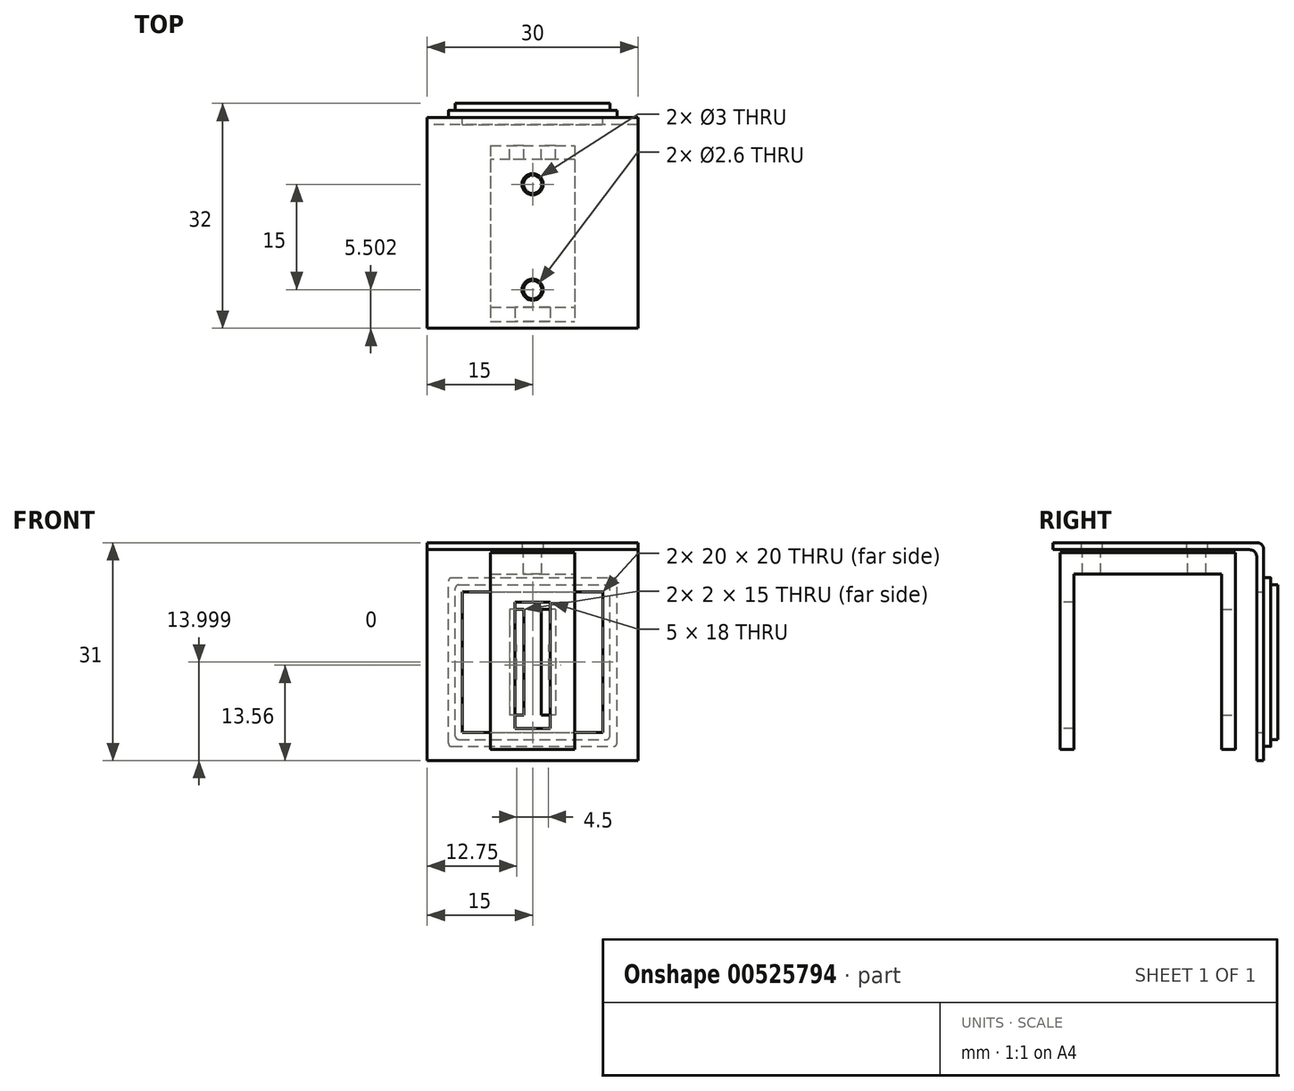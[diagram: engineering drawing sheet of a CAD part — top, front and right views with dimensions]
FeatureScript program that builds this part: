
annotation { "Feature Type Name" : "Feature", "Feature Type Description" : "" }
export const myFeature = defineFeature(function(context is Context, id is Id, definition is map)
    precondition{}
    {
        {
            var Q0;
            Q0=qCreatedBy(makeId("Right.planeOp"),FACE);
            var sketch = newSketch(context, id + "F0", { "sketchPlane" : qUnion([Q0])});
            skLineSegment(sketch, "E0.bottom", {"start": v(-2.16, 1.44) * mm, "end": v(27.84, 1.44) * mm});
            skLineSegment(sketch, "E0.top", {"start": v(-2.16, 0.44) * mm, "end": v(27.84, 0.44) * mm});
            skLineSegment(sketch, "E0.left", {"start": v(-2.16, 1.44) * mm, "end": v(-2.16, 0.44) * mm});
            skLineSegment(sketch, "E0.right", {"start": v(27.84, 1.44) * mm, "end": v(27.84, 0.44) * mm});
            skLineSegment(sketch, "E1.bottom", {"start": v(27.84, 0.44) * mm, "end": v(26.84, 0.44) * mm});
            skLineSegment(sketch, "E1.top", {"start": v(27.84, -29.56) * mm, "end": v(26.84, -29.56) * mm});
            skLineSegment(sketch, "E1.left", {"start": v(27.84, 0.44) * mm, "end": v(27.84, -29.56) * mm});
            skLineSegment(sketch, "E1.right", {"start": v(26.84, 0.44) * mm, "end": v(26.84, -29.56) * mm});
            skSolve(sketch);
        }
        {
            var Q0;
            Q0=qSketchRegion(id+"F0",true);
            extrude(context, id + "F1", {"entities" : qUnion([Q0]), "depth" : 30 * mm});
        }
        {
            var Q0;
            Q0=makeQuery(id+"F1.opExtrude","SWEPT_EDGE",EDGE,{"disambiguationData":[OSD([sQuery(id+"F0.wireOp",EDGE,"E0.bottom"),sQuery(id+"F0.wireOp",EDGE,"E0.right")])]});
            var Q1;
            Q1=makeQuery(id+"F1.opExtrude","SWEPT_EDGE",EDGE,{"disambiguationData":[OSD([sQuery(id+"F0.wireOp",EDGE,"E0.top"),sQuery(id+"F0.wireOp",EDGE,"E1.bottom"),sQuery(id+"F0.wireOp",EDGE,"E1.right")])]});
            fillet(context, id + "F2", {"entities" : qUnion([Q0, Q1]), "radius" : 1 * mm, "tangentPropagation" : true, "allowEdgeOverflow" : false});
        }
        {
            var Q0;
            Q0=makeQuery(id+"F1.opExtrude","SWEPT_FACE",FACE,{"disambiguationData":[OSD([sQuery(id+"F0.wireOp",EDGE,"E0.right"),sQuery(id+"F0.wireOp",EDGE,"E1.left")])]});
            var sketch = newSketch(context, id + "F3", { "sketchPlane" : qUnion([Q0])});
            skLineSegment(sketch, "E2.bottom", {"start": v(-5, -25.56) * mm, "end": v(-25, -25.56) * mm});
            skLineSegment(sketch, "E2.top", {"start": v(-5, -5.56) * mm, "end": v(-25, -5.56) * mm});
            skLineSegment(sketch, "E2.left", {"start": v(-5, -25.56) * mm, "end": v(-5, -5.56) * mm});
            skLineSegment(sketch, "E2.right", {"start": v(-25, -25.56) * mm, "end": v(-25, -5.56) * mm});
            skPoint(sketch, "E2.middle", {"position": v(-15, -15.56) * mm});
            skPoint(sketch, "E3", {"position": v(-15, -29.56) * mm});
            skSolve(sketch);
        }
        {
            var Q0;
            Q0=qSketchRegion(id+"F3",true);
            extrude(context, id + "F4", {"entities" : qUnion([Q0]), "operationType" : NewBodyOperationType.REMOVE, "oppositeDirection" : true, "depth" : 1 * mm});
        }
        {
            var Q0;
            Q0=makeQuery(id+"F1.opExtrude","SWEPT_FACE",FACE,{"disambiguationData":[OSD([sQuery(id+"F0.wireOp",EDGE,"E0.bottom")])]});
            var sketch = newSketch(context, id + "F5", { "sketchPlane" : qUnion([Q0])});
            skCircle(sketch, "E4", {"center": v(15, 18.34) * mm, "radius": 1.5 * mm});
            skPoint(sketch, "E4.centerSnap0", {"position": v(15, 26.84) * mm});
            skCircle(sketch, "E5", {"center": v(15, 3.34) * mm, "radius": 1.5 * mm});
            skSolve(sketch);
        }
        {
            var Q0;
            Q0=sQuery(id+"F5.wireOp",VERTEX,"E5.center");
            var Q1;
            Q1=sQuery(id+"F5.wireOp",VERTEX,"E4.center");
            var Q2;
            Q2=makeQuery(id+"F1.opExtrude","SWEPT_BODY",BODY,{"disambiguationData":[OSD([sQuery(id+"F0.wireOp",EDGE,"E0.bottom"),sQuery(id+"F0.wireOp",EDGE,"E0.top"),sQuery(id+"F0.wireOp",EDGE,"E0.left"),sQuery(id+"F0.wireOp",EDGE,"E0.right"),sQuery(id+"F0.wireOp",EDGE,"E1.top"),sQuery(id+"F0.wireOp",EDGE,"E1.left"),sQuery(id+"F0.wireOp",EDGE,"E1.right")])]});
            hole(context, id + "F6", {"style" : HoleStyle.SIMPLE, "endStyle" : HoleEndStyle.BLIND, "holeDiameter" : 3 * mm, "holeDepth" : 1 * mm, "tappedDepth" : 12 * mm, "tapClearance" : 3, "locations" : qUnion([Q0, Q1]), "scope" : qUnion([Q2])});
        }
        {
            var Q0;
            Q0=qCreatedBy(makeId("Top.planeOp"),FACE);
            var sketch = newSketch(context, id + "F7", { "sketchPlane" : qUnion([Q0])});
            skLineSegment(sketch, "E6.bottom", {"start": v(9, 23.84) * mm, "end": v(21, 23.84) * mm});
            skLineSegment(sketch, "E6.top", {"start": v(9, -1.16) * mm, "end": v(21, -1.16) * mm});
            skLineSegment(sketch, "E6.left", {"start": v(9, 23.84) * mm, "end": v(9, -1.16) * mm});
            skLineSegment(sketch, "E6.right", {"start": v(21, 23.84) * mm, "end": v(21, -1.16) * mm});
            skPoint(sketch, "E6.middle", {"position": v(15, 11.34) * mm});
            skCircle(sketch, "E7", {"center": v(15, 18.34) * mm, "radius": 1.3 * mm});
            skCircle(sketch, "E8", {"center": v(15, 3.34) * mm, "radius": 1.3 * mm});
            skSolve(sketch);
        }
        {
            var Q0;
            Q0=qSketchRegion(id+"F7",true);
            extrude(context, id + "F8", {"entities" : qUnion([Q0]), "oppositeDirection" : true, "depth" : 3 * mm});
        }
        {
            var Q0;
            Q0=makeQuery(id+"F8.opExtrude","CAP_FACE",FACE,{"disambiguationData":[OSD([sQuery(id+"F7.wireOp",EDGE,"E6.bottom"),sQuery(id+"F7.wireOp",EDGE,"E6.top"),sQuery(id+"F7.wireOp",EDGE,"E6.left"),sQuery(id+"F7.wireOp",EDGE,"E6.right")])],"isStart":false});
            var sketch = newSketch(context, id + "F9", { "sketchPlane" : qUnion([Q0])});
            skLineSegment(sketch, "E9.bottom", {"start": v(21, -23.84) * mm, "end": v(9, -23.84) * mm});
            skLineSegment(sketch, "E9.top", {"start": v(21, -21.84) * mm, "end": v(9, -21.84) * mm});
            skLineSegment(sketch, "E9.left", {"start": v(21, -23.84) * mm, "end": v(21, -21.84) * mm});
            skLineSegment(sketch, "E9.right", {"start": v(9, -23.84) * mm, "end": v(9, -21.84) * mm});
            skLineSegment(sketch, "E10.bottom", {"start": v(9, 1.16) * mm, "end": v(21, 1.16) * mm});
            skLineSegment(sketch, "E10.top", {"start": v(9, -0.84) * mm, "end": v(21, -0.84) * mm});
            skLineSegment(sketch, "E10.left", {"start": v(9, 1.16) * mm, "end": v(9, -0.84) * mm});
            skLineSegment(sketch, "E10.right", {"start": v(21, 1.16) * mm, "end": v(21, -0.84) * mm});
            skSolve(sketch);
        }
        {
            var Q0;
            Q0=qSketchRegion(id+"F9",true);
            extrude(context, id + "F10", {"entities" : qUnion([Q0]), "operationType" : NewBodyOperationType.ADD, "depth" : 25 * mm});
        }
        {
            var Q0;
            Q0=makeQuery(id+"F10.boolean.opBoolean","MERGE",FACE,{"derivedFrom":[makeQuery(id+"F8.opExtrude","SWEPT_FACE",FACE,{"disambiguationData":[OSD([sQuery(id+"F7.wireOp",EDGE,"E6.bottom")])]}),makeQuery(id+"F10.opExtrude","SWEPT_FACE",FACE,{"disambiguationData":[OSD([sQuery(id+"F9.wireOp",EDGE,"E9.bottom")])]})]});
            var sketch = newSketch(context, id + "F11", { "sketchPlane" : qUnion([Q0])});
            skLineSegment(sketch, "E11.bottom", {"start": v(-18.25, -8.06) * mm, "end": v(-16.25, -8.06) * mm});
            skLineSegment(sketch, "E11.top", {"start": v(-18.25, -23.06) * mm, "end": v(-16.25, -23.06) * mm});
            skLineSegment(sketch, "E11.left", {"start": v(-18.25, -8.06) * mm, "end": v(-18.25, -23.06) * mm});
            skLineSegment(sketch, "E11.right", {"start": v(-16.25, -8.06) * mm, "end": v(-16.25, -23.06) * mm});
            skLineSegment(sketch, "E12.bottom", {"start": v(-13.75, -8.06) * mm, "end": v(-11.75, -8.06) * mm});
            skLineSegment(sketch, "E12.top", {"start": v(-13.75, -23.06) * mm, "end": v(-11.75, -23.06) * mm});
            skLineSegment(sketch, "E12.left", {"start": v(-13.75, -8.06) * mm, "end": v(-13.75, -23.06) * mm});
            skLineSegment(sketch, "E12.right", {"start": v(-11.75, -8.06) * mm, "end": v(-11.75, -23.06) * mm});
            skSolve(sketch);
        }
        {
            var Q0;
            Q0=qSketchRegion(id+"F11",true);
            extrude(context, id + "F12", {"entities" : qUnion([Q0]), "operationType" : NewBodyOperationType.REMOVE, "oppositeDirection" : true, "depth" : 3 * mm});
        }
        {
            var Q0;
            Q0=makeQuery(id+"F10.boolean.opBoolean","MERGE",FACE,{"derivedFrom":[makeQuery(id+"F8.opExtrude","SWEPT_FACE",FACE,{"disambiguationData":[OSD([sQuery(id+"F7.wireOp",EDGE,"E6.top")])]}),makeQuery(id+"F10.opExtrude","SWEPT_FACE",FACE,{"disambiguationData":[OSD([sQuery(id+"F9.wireOp",EDGE,"E10.bottom")])]})]});
            var sketch = newSketch(context, id + "F13", { "sketchPlane" : qUnion([Q0])});
            skLineSegment(sketch, "E13.bottom", {"start": v(17.5, -25) * mm, "end": v(12.5, -25) * mm});
            skLineSegment(sketch, "E13.top", {"start": v(17.5, -7) * mm, "end": v(12.5, -7) * mm});
            skLineSegment(sketch, "E13.left", {"start": v(17.5, -25) * mm, "end": v(17.5, -7) * mm});
            skLineSegment(sketch, "E13.right", {"start": v(12.5, -25) * mm, "end": v(12.5, -7) * mm});
            skPoint(sketch, "E13.middle", {"position": v(15, -16) * mm});
            skPoint(sketch, "E13.middle.positionSnap0", {"position": v(15, 0) * mm});
            skPoint(sketch, "E13.centerSnap0", {"position": v(15, 0) * mm});
            skSolve(sketch);
        }
        {
            var Q0;
            Q0=qSketchRegion(id+"F13",true);
            extrude(context, id + "F14", {"entities" : qUnion([Q0]), "operationType" : NewBodyOperationType.REMOVE, "oppositeDirection" : true, "depth" : 2 * mm});
        }
        {
            var Q0;
            Q0=makeQuery(id+"F1.opExtrude","SWEPT_FACE",FACE,{"disambiguationData":[OSD([sQuery(id+"F0.wireOp",EDGE,"E0.right"),sQuery(id+"F0.wireOp",EDGE,"E1.left")])]});
            var sketch = newSketch(context, id + "F15", { "sketchPlane" : qUnion([Q0])});
            skLineSegment(sketch, "E14.bottom", {"start": v(-5, -25.56) * mm, "end": v(-25, -25.56) * mm});
            skLineSegment(sketch, "E14.top", {"start": v(-5, -5.56) * mm, "end": v(-25, -5.56) * mm});
            skLineSegment(sketch, "E14.left", {"start": v(-5, -25.56) * mm, "end": v(-5, -5.56) * mm});
            skLineSegment(sketch, "E14.right", {"start": v(-25, -25.56) * mm, "end": v(-25, -5.56) * mm});
            skPoint(sketch, "E14.middle", {"position": v(-15, -15.56) * mm});
            skPoint(sketch, "E14.middle.positionSnap0", {"position": v(-25, -15.56) * mm});
            skPoint(sketch, "E14.middle.positionSnap1", {"position": v(-15, -5.56) * mm});
            skPoint(sketch, "E14.centerSnap0", {"position": v(-25, -15.56) * mm});
            skPoint(sketch, "E14.centerSnap1", {"position": v(-15, -5.56) * mm});
            skLineSegment(sketch, "E15.bottom", {"start": v(-3, -27.56) * mm, "end": v(-27, -27.56) * mm});
            skLineSegment(sketch, "E15.top", {"start": v(-3, -3.56) * mm, "end": v(-27, -3.56) * mm});
            skLineSegment(sketch, "E15.left", {"start": v(-3, -27.56) * mm, "end": v(-3, -3.56) * mm});
            skLineSegment(sketch, "E15.right", {"start": v(-27, -27.56) * mm, "end": v(-27, -3.56) * mm});
            skSolve(sketch);
        }
        {
            var Q0;
            Q0=qSketchRegion(id+"F15",true);
            extrude(context, id + "F16", {"entities" : qUnion([Q0]), "depth" : 2 * mm});
        }
        {
            var Q0;
            Q0=makeQuery(id+"F16.opExtrude","CAP_FACE",FACE,{"disambiguationData":[OSD([sQuery(id+"F15.wireOp",EDGE,"E14.bottom"),sQuery(id+"F15.wireOp",EDGE,"E14.top"),sQuery(id+"F15.wireOp",EDGE,"E14.left"),sQuery(id+"F15.wireOp",EDGE,"E14.right"),sQuery(id+"F15.wireOp",EDGE,"E15.bottom"),sQuery(id+"F15.wireOp",EDGE,"E15.top"),sQuery(id+"F15.wireOp",EDGE,"E15.left"),sQuery(id+"F15.wireOp",EDGE,"E15.right")])],"isStart":false});
            var sketch = newSketch(context, id + "F17", { "sketchPlane" : qUnion([Q0])});
            skLineSegment(sketch, "E16.bottom", {"start": v(-3, -27.56) * mm, "end": v(-27, -27.56) * mm});
            skLineSegment(sketch, "E16.top", {"start": v(-3, -3.56) * mm, "end": v(-27, -3.56) * mm});
            skLineSegment(sketch, "E16.left", {"start": v(-3, -27.56) * mm, "end": v(-3, -3.56) * mm});
            skLineSegment(sketch, "E16.right", {"start": v(-27, -27.56) * mm, "end": v(-27, -3.56) * mm});
            skPoint(sketch, "E16.middle", {"position": v(-15, -15.56) * mm});
            skPoint(sketch, "E16.middle.positionSnap0", {"position": v(-25, -15.56) * mm});
            skPoint(sketch, "E16.middle.positionSnap1", {"position": v(-15, -5.56) * mm});
            skPoint(sketch, "E16.centerSnap0", {"position": v(-25, -15.56) * mm});
            skPoint(sketch, "E16.centerSnap1", {"position": v(-15, -5.56) * mm});
            skLineSegment(sketch, "E17.bottom", {"start": v(-4, -26.56) * mm, "end": v(-26, -26.56) * mm});
            skLineSegment(sketch, "E17.top", {"start": v(-4, -4.56) * mm, "end": v(-26, -4.56) * mm});
            skLineSegment(sketch, "E17.left", {"start": v(-4, -26.56) * mm, "end": v(-4, -4.56) * mm});
            skLineSegment(sketch, "E17.right", {"start": v(-26, -26.56) * mm, "end": v(-26, -4.56) * mm});
            skSolve(sketch);
        }
        {
            var Q0;
            Q0=qSketchRegion(id+"F17",true);
            extrude(context, id + "F18", {"entities" : qUnion([Q0]), "operationType" : NewBodyOperationType.REMOVE, "oppositeDirection" : true, "depth" : 1 * mm});
        }
        {
            var Q0;
            Q0=makeQuery(id+"F18.boolean.opBoolean","COPY",EDGE,{"derivedFrom":makeQuery(id+"F18.opExtrude","SWEPT_EDGE",EDGE,{"disambiguationData":[OSD([sQuery(id+"F17.wireOp",EDGE,"E17.top"),sQuery(id+"F17.wireOp",EDGE,"E17.right")])]})});
            var Q1;
            Q1=makeQuery(id+"F18.boolean.opBoolean","COPY",EDGE,{"derivedFrom":makeQuery(id+"F18.opExtrude","SWEPT_EDGE",EDGE,{"disambiguationData":[OSD([sQuery(id+"F17.wireOp",EDGE,"E17.top"),sQuery(id+"F17.wireOp",EDGE,"E17.left")])]})});
            var Q2;
            Q2=makeQuery(id+"F18.boolean.opBoolean","COPY",EDGE,{"derivedFrom":makeQuery(id+"F18.opExtrude","SWEPT_EDGE",EDGE,{"disambiguationData":[OSD([sQuery(id+"F17.wireOp",EDGE,"E17.bottom"),sQuery(id+"F17.wireOp",EDGE,"E17.left")])]})});
            var Q3;
            Q3=makeQuery(id+"F18.boolean.opBoolean","COPY",EDGE,{"derivedFrom":makeQuery(id+"F18.opExtrude","SWEPT_EDGE",EDGE,{"disambiguationData":[OSD([sQuery(id+"F17.wireOp",EDGE,"E17.bottom"),sQuery(id+"F17.wireOp",EDGE,"E17.right")])]})});
            var Q4;
            Q4=makeQuery(id+"F16.opExtrude","SWEPT_EDGE",EDGE,{"disambiguationData":[OSD([sQuery(id+"F15.wireOp",EDGE,"E15.top"),sQuery(id+"F15.wireOp",EDGE,"E15.right")])]});
            var Q5;
            Q5=makeQuery(id+"F16.opExtrude","SWEPT_EDGE",EDGE,{"disambiguationData":[OSD([sQuery(id+"F15.wireOp",EDGE,"E15.top"),sQuery(id+"F15.wireOp",EDGE,"E15.left")])]});
            var Q6;
            Q6=makeQuery(id+"F16.opExtrude","SWEPT_EDGE",EDGE,{"disambiguationData":[OSD([sQuery(id+"F15.wireOp",EDGE,"E15.bottom"),sQuery(id+"F15.wireOp",EDGE,"E15.right")])]});
            var Q7;
            Q7=makeQuery(id+"F16.opExtrude","SWEPT_EDGE",EDGE,{"disambiguationData":[OSD([sQuery(id+"F15.wireOp",EDGE,"E15.bottom"),sQuery(id+"F15.wireOp",EDGE,"E15.left")])]});
            fillet(context, id + "F19", {"entities" : qUnion([Q0, Q1, Q2, Q3, Q4, Q5, Q6, Q7]), "radius" : 0.5 * mm, "tangentPropagation" : true, "allowEdgeOverflow" : false});
        }
    });
